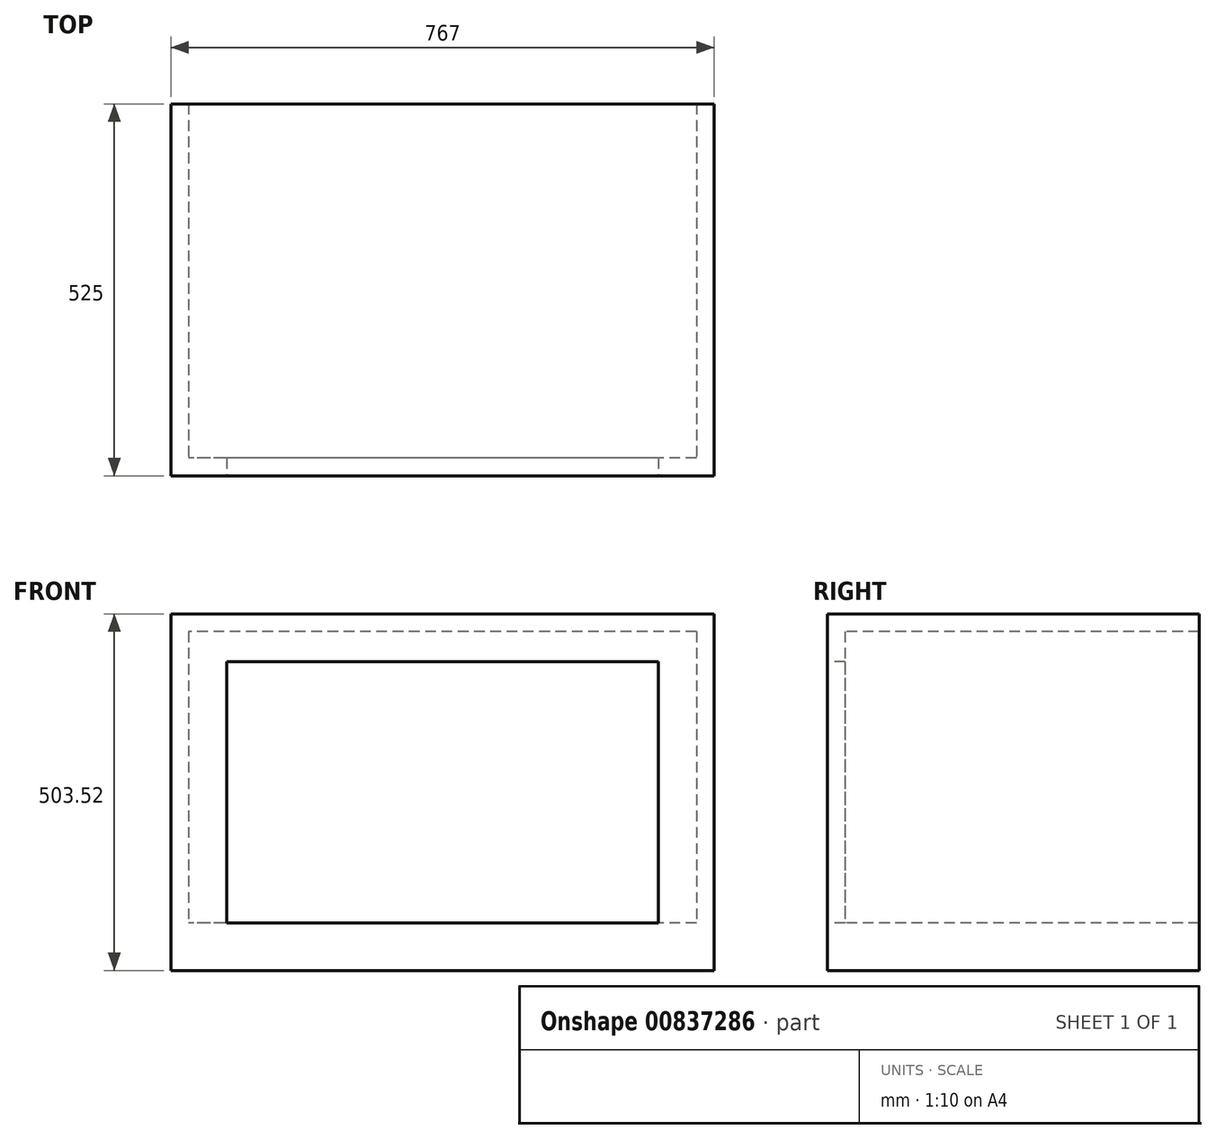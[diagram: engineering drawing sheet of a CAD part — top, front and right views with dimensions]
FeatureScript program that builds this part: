
annotation { "Feature Type Name" : "Feature", "Feature Type Description" : "" }
export const myFeature = defineFeature(function(context is Context, id is Id, definition is map)
    precondition{}
    {
        {
            var Q0;
            Q0=qCreatedBy(makeId("Front.planeOp"),FACE);
            var sketch = newSketch(context, id + "F0", { "sketchPlane" : qUnion([Q0])});
            skLineSegment(sketch, "E0.bottom", {"start": v(305, 184.5) * mm, "end": v(-305, 184.5) * mm});
            skLineSegment(sketch, "E0.top", {"start": v(305, -184.5) * mm, "end": v(-305, -184.5) * mm});
            skLineSegment(sketch, "E0.left", {"start": v(305, 184.5) * mm, "end": v(305, -184.5) * mm});
            skLineSegment(sketch, "E0.right", {"start": v(-305, 184.5) * mm, "end": v(-305, -184.5) * mm});
            skPoint(sketch, "E0.middle", {"position": v(0, 0) * mm});
            skLineSegment(sketch, "E1.bottom", {"start": v(383.5, 251.76) * mm, "end": v(-383.5, 251.76) * mm});
            skLineSegment(sketch, "E1.top", {"start": v(383.5, -251.76) * mm, "end": v(-383.5, -251.76) * mm});
            skLineSegment(sketch, "E1.left", {"start": v(383.5, 251.76) * mm, "end": v(383.5, -251.76) * mm});
            skLineSegment(sketch, "E1.right", {"start": v(-383.5, 251.76) * mm, "end": v(-383.5, -251.76) * mm});
            skSolve(sketch);
        }
        {
            var Q0;
            Q0=makeQuery(id+"F0.imprint","IMPRINT",FACE,{"disambiguationData":[TD([[makeQuery(id+"F0.imprint","IMPRINT",EDGE,{"derivedFrom":sQuery(id+"F0.wireOp",EDGE,"E0.bottom")}),-1.0]])]});
            extrude(context, id + "F1", {"entities" : qUnion([Q0]), "oppositeDirection" : true, "depth" : 25 * mm, "offsetDistance" : 25 * mm});
        }
        {
            var Q0;
            Q0=makeQuery(id+"F1.opExtrude","CAP_FACE",FACE,{"disambiguationData":[OSD([sQuery(id+"F0.wireOp",EDGE,"E0.bottom"),sQuery(id+"F0.wireOp",EDGE,"E0.top"),sQuery(id+"F0.wireOp",EDGE,"E0.left"),sQuery(id+"F0.wireOp",EDGE,"E0.right"),sQuery(id+"F0.wireOp",EDGE,"E1.bottom"),sQuery(id+"F0.wireOp",EDGE,"E1.top"),sQuery(id+"F0.wireOp",EDGE,"E1.left"),sQuery(id+"F0.wireOp",EDGE,"E1.right")])],"isStart":false});
            var sketch = newSketch(context, id + "F2", { "sketchPlane" : qUnion([Q0])});
            skLineSegment(sketch, "E2.bottom", {"start": v(-358.5, 226.76) * mm, "end": v(358.5, 226.76) * mm});
            skLineSegment(sketch, "E2.top", {"start": v(-358.5, -184.5) * mm, "end": v(358.5, -184.5) * mm});
            skLineSegment(sketch, "E2.left", {"start": v(-358.5, 226.76) * mm, "end": v(-358.5, -184.5) * mm});
            skLineSegment(sketch, "E2.right", {"start": v(358.5, 226.76) * mm, "end": v(358.5, -184.5) * mm});
            skSolve(sketch);
        }
        {
            var Q0;
            Q0=makeQuery(id+"F2.imprint","IMPRINT",FACE,{"disambiguationData":[TD([[makeQuery(id+"F2.imprint","IMPRINT",EDGE,{"derivedFrom":sQuery(id+"F2.wireOp",EDGE,"E2.bottom")}),1.0]])]});
            extrude(context, id + "F3", {"entities" : qUnion([Q0]), "operationType" : NewBodyOperationType.ADD, "depth" : 500 * mm, "offsetDistance" : 25 * mm});
        }
    });
